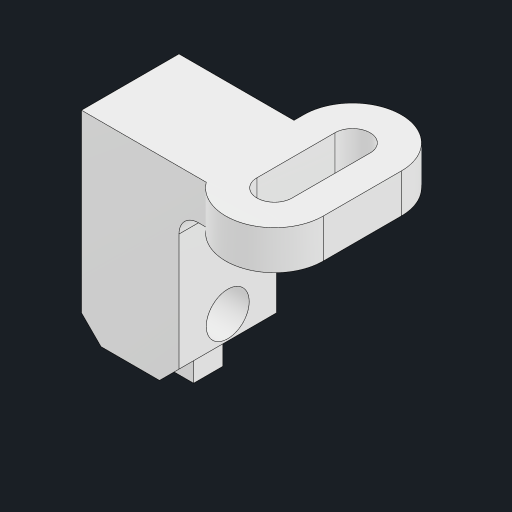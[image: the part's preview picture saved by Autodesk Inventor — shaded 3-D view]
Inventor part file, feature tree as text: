
AUTODESK INVENTOR PART (.ipt)
format: ipt  version: 2023 (Build 270158000, 158)  size: 168,960 bytes
history: native  units: mm
features: sketch x3, extrude x3, other x2, hole x1, fillet x1, chamfer x1
ambient origin geometry x8: Origin, YZ Plane, XZ Plane, XY Plane, X Axis, Y Axis, Z Axis, Center Point
bodies: Body1 (feature_tree)
feature tree (11):
  other  "ソリッド1"
  sketch  "スケッチ1"
  extrude  "押し出し1"  Depth=1.8mm
  extrude  "押し出し4"  Depth=4.0mm
  hole  "穴2"  [1 undecoded]
  fillet  "フィレット2"  Radius=2.0mm
  other  "作業平面2"
  chamfer  "面取り1"  Distance=5.0mm
  extrude  "押し出し5"  Depth=5.9mm
  sketch  "スケッチ5"
  sketch  "スケッチ6"
note: 1 required parameter value undecoded (feature->parameter linkage not recoverable at this tier; creation-order binding heuristic only, values carry confidence <= 0.55)
